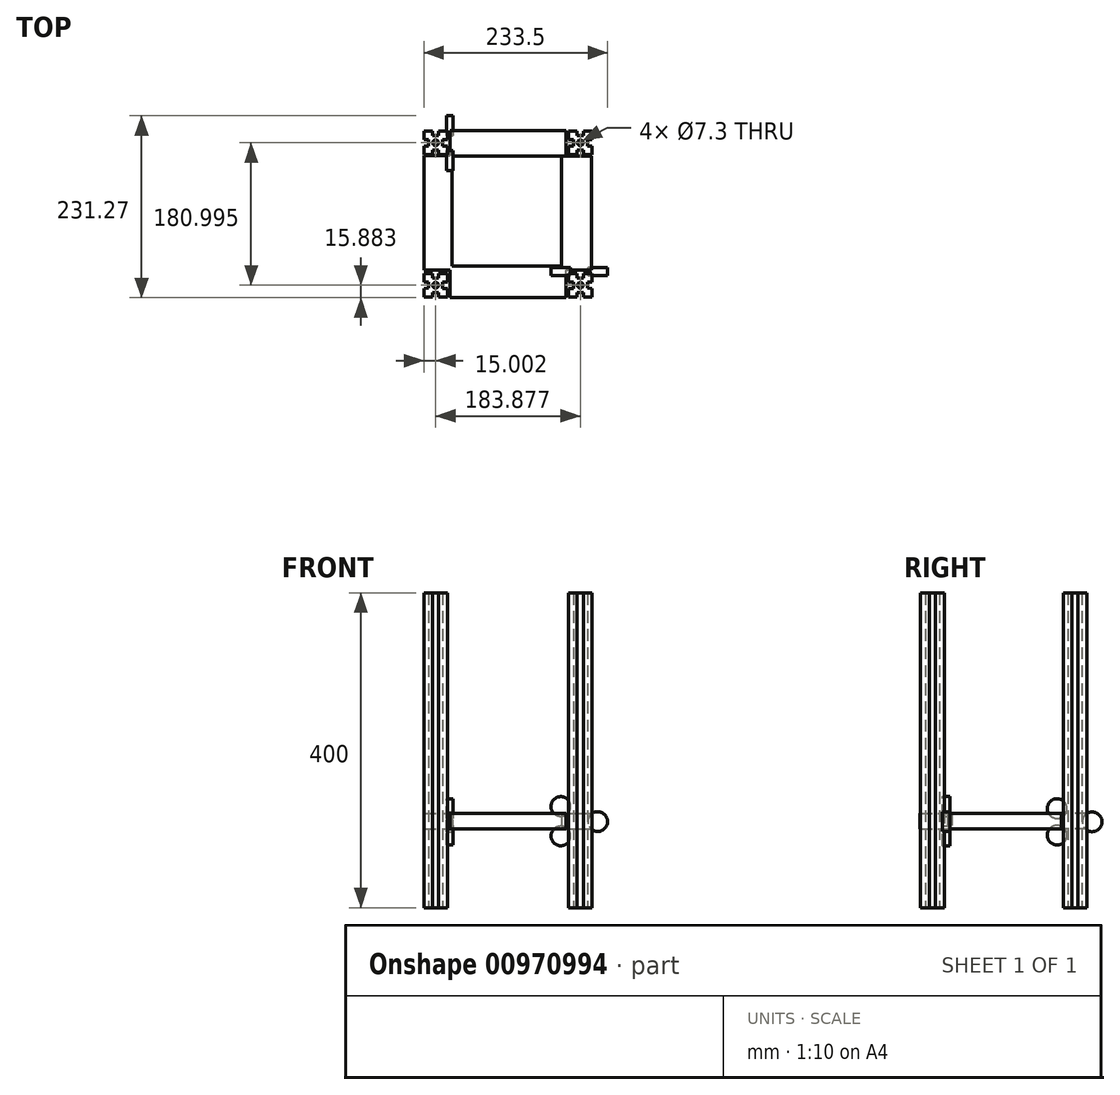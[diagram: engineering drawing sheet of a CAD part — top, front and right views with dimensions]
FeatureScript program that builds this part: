
annotation { "Feature Type Name" : "Feature", "Feature Type Description" : "" }
export const myFeature = defineFeature(function(context is Context, id is Id, definition is map)
    precondition{}
    {
        {
            var Q0;
            Q0=qCreatedBy(makeId("Top.planeOp"),FACE);
            var sketch = newSketch(context, id + "F0", { "sketchPlane" : qUnion([Q0])});
            skLineSegment(sketch, "E0.bottom", {"start": v(87.94, -105.5) * mm, "end": v(76.94, -105.5) * mm});
            skLineSegment(sketch, "E0.top", {"start": v(106.94, -75.5) * mm, "end": v(95.94, -75.5) * mm});
            skLineSegment(sketch, "E1.bottom", {"start": v(82.94, -81.5) * mm, "end": v(100.94, -81.5) * mm});
            skLineSegment(sketch, "E1.top", {"start": v(82.94, -99.5) * mm, "end": v(100.94, -99.5) * mm});
            skLineSegment(sketch, "E1.left", {"start": v(82.94, -81.5) * mm, "end": v(82.94, -99.5) * mm});
            skLineSegment(sketch, "E1.right", {"start": v(100.94, -81.5) * mm, "end": v(100.94, -99.5) * mm});
            skLineSegment(sketch, "E2", {"start": v(82.94, -81.5) * mm, "end": v(100.94, -99.5) * mm, "construction": true});
            skLineSegment(sketch, "E3", {"start": v(100.94, -81.5) * mm, "end": v(82.94, -99.5) * mm, "construction": true});
            skCircle(sketch, "E4", {"center": v(91.94, -90.5) * mm, "radius": 3.65 * mm});
            skLineSegment(sketch, "E5", {"start": v(95.94, -75.5) * mm, "end": v(106.94, -75.5) * mm});
            skPoint(sketch, "E6.start.orphan", {"position": v(91.94, -75.5) * mm});
            skLineSegment(sketch, "E7", {"start": v(76.94, -75.5) * mm, "end": v(87.94, -75.5) * mm});
            skPoint(sketch, "E8.start.orphan", {"position": v(87.94, -105.5) * mm});
            skLineSegment(sketch, "E9", {"start": v(106.94, -105.5) * mm, "end": v(95.94, -105.5) * mm});
            skLineSegment(sketch, "E10", {"start": v(106.94, -75.5) * mm, "end": v(106.94, -86.5) * mm});
            skLineSegment(sketch, "E11", {"start": v(106.94, -105.5) * mm, "end": v(106.94, -94.5) * mm});
            skLineSegment(sketch, "E12", {"start": v(76.94, -75.5) * mm, "end": v(76.94, -86.5) * mm});
            skLineSegment(sketch, "E13", {"start": v(76.94, -94.5) * mm, "end": v(76.94, -105.5) * mm});
            skLineSegment(sketch, "E14", {"start": v(95.94, -75.5) * mm, "end": v(95.94, -81.5) * mm});
            skLineSegment(sketch, "E15", {"start": v(95.94, -81.5) * mm, "end": v(87.94, -81.5) * mm});
            skLineSegment(sketch, "E16", {"start": v(87.94, -81.5) * mm, "end": v(87.94, -75.5) * mm});
            skLineSegment(sketch, "E17", {"start": v(76.94, -86.5) * mm, "end": v(82.94, -86.5) * mm});
            skLineSegment(sketch, "E18", {"start": v(82.94, -86.5) * mm, "end": v(82.94, -94.5) * mm});
            skLineSegment(sketch, "E19", {"start": v(82.94, -94.5) * mm, "end": v(76.94, -94.5) * mm});
            skLineSegment(sketch, "E20", {"start": v(87.94, -99.5) * mm, "end": v(87.94, -105.5) * mm});
            skLineSegment(sketch, "E21", {"start": v(95.94, -105.5) * mm, "end": v(95.94, -99.5) * mm});
            skLineSegment(sketch, "E22", {"start": v(106.94, -94.5) * mm, "end": v(100.94, -94.36) * mm});
            skLineSegment(sketch, "E23", {"start": v(100.94, -94.36) * mm, "end": v(100.94, -86.5) * mm});
            skLineSegment(sketch, "E24", {"start": v(100.94, -86.5) * mm, "end": v(106.94, -86.5) * mm});
            skLineSegment(sketch, "E25.MirrorCS", {"start": v(106.94, 75.5) * mm, "end": v(95.94, 75.5) * mm});
            skLineSegment(sketch, "E26.MirrorCS", {"start": v(100.94, 94.36) * mm, "end": v(100.94, 86.5) * mm});
            skLineSegment(sketch, "E27.MirrorCS", {"start": v(106.94, 105.5) * mm, "end": v(106.94, 94.5) * mm});
            skLineSegment(sketch, "E28.MirrorCS", {"start": v(76.94, 86.5) * mm, "end": v(82.94, 86.5) * mm});
            skLineSegment(sketch, "E29.MirrorCS", {"start": v(76.94, 75.5) * mm, "end": v(87.94, 75.5) * mm});
            skLineSegment(sketch, "E30.MirrorCS", {"start": v(106.94, 105.5) * mm, "end": v(95.94, 105.5) * mm});
            skPoint(sketch, "E31.MirrorP", {"position": v(87.94, 105.5) * mm});
            skLineSegment(sketch, "E32.MirrorCS", {"start": v(95.94, 75.5) * mm, "end": v(106.94, 75.5) * mm});
            skLineSegment(sketch, "E33.MirrorCS", {"start": v(76.94, 75.5) * mm, "end": v(76.94, 86.5) * mm});
            skPoint(sketch, "E34.MirrorP", {"position": v(91.94, 75.5) * mm});
            skLineSegment(sketch, "E35.MirrorCS", {"start": v(82.94, 86.5) * mm, "end": v(82.94, 94.5) * mm});
            skLineSegment(sketch, "E36.MirrorCS", {"start": v(95.94, 105.5) * mm, "end": v(95.94, 99.5) * mm});
            skLineSegment(sketch, "E37.MirrorCS", {"start": v(87.94, 105.5) * mm, "end": v(76.94, 105.5) * mm});
            skLineSegment(sketch, "E38.MirrorCS", {"start": v(106.94, 94.5) * mm, "end": v(100.94, 94.36) * mm});
            skLineSegment(sketch, "E39.MirrorCS", {"start": v(95.94, 75.5) * mm, "end": v(95.94, 81.5) * mm});
            skLineSegment(sketch, "E40.MirrorCS", {"start": v(82.94, 94.5) * mm, "end": v(76.94, 94.5) * mm});
            skLineSegment(sketch, "E41.MirrorCS", {"start": v(82.94, 81.5) * mm, "end": v(100.94, 99.5) * mm, "construction": true});
            skLineSegment(sketch, "E42.MirrorCS", {"start": v(82.94, 99.5) * mm, "end": v(100.94, 99.5) * mm});
            skLineSegment(sketch, "E43.MirrorCS", {"start": v(87.94, 99.5) * mm, "end": v(87.94, 105.5) * mm});
            skLineSegment(sketch, "E44.MirrorCS", {"start": v(76.94, 94.5) * mm, "end": v(76.94, 105.5) * mm});
            skCircle(sketch, "E45.MirrorC", {"center": v(91.94, 90.5) * mm, "radius": 3.65 * mm});
            skLineSegment(sketch, "E46.MirrorCS", {"start": v(95.94, 81.5) * mm, "end": v(87.94, 81.5) * mm});
            skLineSegment(sketch, "E47.MirrorCS", {"start": v(100.94, 81.5) * mm, "end": v(82.94, 99.5) * mm, "construction": true});
            skLineSegment(sketch, "E48.MirrorCS", {"start": v(87.94, 81.5) * mm, "end": v(87.94, 75.5) * mm});
            skLineSegment(sketch, "E49.MirrorCS", {"start": v(100.94, 86.5) * mm, "end": v(106.94, 86.5) * mm});
            skLineSegment(sketch, "E50.MirrorCS", {"start": v(100.94, 81.5) * mm, "end": v(100.94, 99.5) * mm});
            skLineSegment(sketch, "E51.MirrorCS", {"start": v(82.94, 81.5) * mm, "end": v(82.94, 99.5) * mm});
            skLineSegment(sketch, "E52.MirrorCS", {"start": v(82.94, 81.5) * mm, "end": v(100.94, 81.5) * mm});
            skLineSegment(sketch, "E53.MirrorCS", {"start": v(106.94, 75.5) * mm, "end": v(106.94, 86.5) * mm});
            skLineSegment(sketch, "E54.MirrorCS", {"start": v(-100.94, -94.36) * mm, "end": v(-100.94, -86.5) * mm});
            skLineSegment(sketch, "E55.MirrorCS", {"start": v(-106.94, -94.5) * mm, "end": v(-100.94, -94.36) * mm});
            skLineSegment(sketch, "E56.MirrorCS", {"start": v(-100.94, -86.5) * mm, "end": v(-106.94, -86.5) * mm});
            skLineSegment(sketch, "E57.MirrorCS", {"start": v(-100.94, -81.5) * mm, "end": v(-100.94, -99.5) * mm});
            skLineSegment(sketch, "E58.MirrorCS", {"start": v(-82.94, -81.5) * mm, "end": v(-100.94, -81.5) * mm});
            skLineSegment(sketch, "E59.MirrorCS", {"start": v(-106.94, -75.5) * mm, "end": v(-95.94, -75.5) * mm});
            skLineSegment(sketch, "E60.MirrorCS", {"start": v(-76.94, -75.5) * mm, "end": v(-76.94, -86.5) * mm});
            skLineSegment(sketch, "E61.MirrorCS", {"start": v(-106.94, -75.5) * mm, "end": v(-106.94, -86.5) * mm});
            skLineSegment(sketch, "E62.MirrorCS", {"start": v(-95.94, -75.5) * mm, "end": v(-95.94, -81.5) * mm});
            skLineSegment(sketch, "E63.MirrorCS", {"start": v(-95.94, -75.5) * mm, "end": v(-106.94, -75.5) * mm});
            skLineSegment(sketch, "E64.MirrorCS", {"start": v(-82.94, 81.5) * mm, "end": v(-100.94, 81.5) * mm});
            skLineSegment(sketch, "E65.MirrorCS", {"start": v(-76.94, -86.5) * mm, "end": v(-82.94, -86.5) * mm});
            skLineSegment(sketch, "E66.MirrorCS", {"start": v(-76.94, -75.5) * mm, "end": v(-87.94, -75.5) * mm});
            skLineSegment(sketch, "E67.MirrorCS", {"start": v(-87.94, -81.5) * mm, "end": v(-87.94, -75.5) * mm});
            skLineSegment(sketch, "E68.MirrorCS", {"start": v(-95.94, -81.5) * mm, "end": v(-87.94, -81.5) * mm});
            skLineSegment(sketch, "E69.MirrorCS", {"start": v(-82.94, -81.5) * mm, "end": v(-82.94, -99.5) * mm});
            skLineSegment(sketch, "E70.MirrorCS", {"start": v(-106.94, 75.5) * mm, "end": v(-95.94, 75.5) * mm});
            skLineSegment(sketch, "E71.MirrorCS", {"start": v(-95.94, 75.5) * mm, "end": v(-95.94, 81.5) * mm});
            skLineSegment(sketch, "E72.MirrorCS", {"start": v(-82.94, -81.5) * mm, "end": v(-100.94, -99.5) * mm, "construction": true});
            skLineSegment(sketch, "E73.MirrorCS", {"start": v(-95.94, 81.5) * mm, "end": v(-87.94, 81.5) * mm});
            skLineSegment(sketch, "E74.MirrorCS", {"start": v(-100.94, 94.36) * mm, "end": v(-100.94, 86.5) * mm});
            skLineSegment(sketch, "E75.MirrorCS", {"start": v(-82.94, 81.5) * mm, "end": v(-82.94, 99.5) * mm});
            skLineSegment(sketch, "E76.MirrorCS", {"start": v(-76.94, -94.5) * mm, "end": v(-76.94, -105.5) * mm});
            skLineSegment(sketch, "E77.MirrorCS", {"start": v(-82.94, -86.5) * mm, "end": v(-82.94, -94.5) * mm});
            skLineSegment(sketch, "E78.MirrorCS", {"start": v(-82.94, 86.5) * mm, "end": v(-82.94, 94.5) * mm});
            skLineSegment(sketch, "E79.MirrorCS", {"start": v(-100.94, 81.5) * mm, "end": v(-82.94, 99.5) * mm, "construction": true});
            skLineSegment(sketch, "E80.MirrorCS", {"start": v(-100.94, 86.5) * mm, "end": v(-106.94, 86.5) * mm});
            skLineSegment(sketch, "E81.MirrorCS", {"start": v(-106.94, 75.5) * mm, "end": v(-106.94, 86.5) * mm});
            skLineSegment(sketch, "E82.MirrorCS", {"start": v(-106.94, -105.5) * mm, "end": v(-106.94, -94.5) * mm});
            skCircle(sketch, "E83.MirrorC", {"center": v(-91.94, -90.5) * mm, "radius": 3.65 * mm});
            skLineSegment(sketch, "E84.MirrorCS", {"start": v(-82.94, -94.5) * mm, "end": v(-76.94, -94.5) * mm});
            skLineSegment(sketch, "E85.MirrorCS", {"start": v(-100.94, -81.5) * mm, "end": v(-82.94, -99.5) * mm, "construction": true});
            skLineSegment(sketch, "E86.MirrorCS", {"start": v(-95.94, 105.5) * mm, "end": v(-95.94, 99.5) * mm});
            skLineSegment(sketch, "E87.MirrorCS", {"start": v(-106.94, -105.5) * mm, "end": v(-95.94, -105.5) * mm});
            skLineSegment(sketch, "E88.MirrorCS", {"start": v(-100.94, 81.5) * mm, "end": v(-100.94, 99.5) * mm});
            skLineSegment(sketch, "E89.MirrorCS", {"start": v(-82.94, -99.5) * mm, "end": v(-100.94, -99.5) * mm});
            skLineSegment(sketch, "E90.MirrorCS", {"start": v(-95.94, -105.5) * mm, "end": v(-95.94, -99.5) * mm});
            skLineSegment(sketch, "E91.MirrorCS", {"start": v(-87.94, 99.5) * mm, "end": v(-87.94, 105.5) * mm});
            skLineSegment(sketch, "E92.MirrorCS", {"start": v(-87.94, -99.5) * mm, "end": v(-87.94, -105.5) * mm});
            skLineSegment(sketch, "E93.MirrorCS", {"start": v(-87.94, -105.5) * mm, "end": v(-76.94, -105.5) * mm});
            skLineSegment(sketch, "E94.MirrorCS", {"start": v(-87.94, 81.5) * mm, "end": v(-87.94, 75.5) * mm});
            skLineSegment(sketch, "E95.MirrorCS", {"start": v(-106.94, 94.5) * mm, "end": v(-100.94, 94.36) * mm});
            skLineSegment(sketch, "E96.MirrorCS", {"start": v(-82.94, 99.5) * mm, "end": v(-100.94, 99.5) * mm});
            skCircle(sketch, "E97.MirrorC", {"center": v(-91.94, 90.5) * mm, "radius": 3.65 * mm});
            skLineSegment(sketch, "E98.MirrorCS", {"start": v(-82.94, 81.5) * mm, "end": v(-100.94, 99.5) * mm, "construction": true});
            skLineSegment(sketch, "E99.MirrorCS", {"start": v(-76.94, 75.5) * mm, "end": v(-76.94, 86.5) * mm});
            skLineSegment(sketch, "E100.MirrorCS", {"start": v(-76.94, 86.5) * mm, "end": v(-82.94, 86.5) * mm});
            skLineSegment(sketch, "E101.MirrorCS", {"start": v(-87.94, 105.5) * mm, "end": v(-76.94, 105.5) * mm});
            skLineSegment(sketch, "E102.MirrorCS", {"start": v(-106.94, 105.5) * mm, "end": v(-95.94, 105.5) * mm});
            skLineSegment(sketch, "E103.MirrorCS", {"start": v(-95.94, 75.5) * mm, "end": v(-106.94, 75.5) * mm});
            skLineSegment(sketch, "E104.MirrorCS", {"start": v(-106.94, 105.5) * mm, "end": v(-106.94, 94.5) * mm});
            skLineSegment(sketch, "E105.MirrorCS", {"start": v(-76.94, 94.5) * mm, "end": v(-76.94, 105.5) * mm});
            skLineSegment(sketch, "E106.MirrorCS", {"start": v(-82.94, 94.5) * mm, "end": v(-76.94, 94.5) * mm});
            skLineSegment(sketch, "E107.MirrorCS", {"start": v(-76.94, 75.5) * mm, "end": v(-87.94, 75.5) * mm});
            skPoint(sketch, "E108.MirrorP", {"position": v(-87.94, -105.5) * mm});
            skPoint(sketch, "E109.MirrorP", {"position": v(-87.94, 105.5) * mm});
            skPoint(sketch, "E110.MirrorP", {"position": v(-91.94, -75.5) * mm});
            skPoint(sketch, "E111.MirrorP", {"position": v(-91.94, 75.5) * mm});
            skSolve(sketch);
        }
        {
            var Q0;
            {var subQ7=sQuery(id+"F0.wireOp",EDGE,"E86.MirrorCS");var subQ9=sQuery(id+"F0.wireOp",EDGE,"E91.MirrorCS");var subQ11=sQuery(id+"F0.wireOp",EDGE,"E74.MirrorCS");var subQ16=sQuery(id+"F0.wireOp",EDGE,"E94.MirrorCS");var subQ50=sQuery(id+"F0.wireOp",EDGE,"E54.MirrorCS");var subQ51=sQuery(id+"F0.wireOp",EDGE,"E55.MirrorCS");var subQ54=sQuery(id+"F0.wireOp",EDGE,"E56.MirrorCS");var subQ73=sQuery(id+"F0.wireOp",EDGE,"E26.MirrorCS");var subQ81=sQuery(id+"F0.wireOp",EDGE,"E28.MirrorCS");Q0=qUnion([makeQuery(id+"F0.imprint","IMPRINT",FACE,{"disambiguationData":[TD([[makeQuery(id+"F0.imprint","IMPRINT",EDGE,{"derivedFrom":sQuery(id+"F0.wireOp",EDGE,"E9")}),-1.0]])]}),makeQuery(id+"F0.imprint","IMPRINT",FACE,{"disambiguationData":[TD([[makeQuery(id+"F0.imprint","IMPRINT",EDGE,{"derivedFrom":sQuery(id+"F0.wireOp",EDGE,"E0.bottom")}),-1.0]])]}),makeQuery(id+"F0.imprint","IMPRINT",FACE,{"disambiguationData":[TD([[makeQuery(id+"F0.imprint","IMPRINT",EDGE,{"derivedFrom":sQuery(id+"F0.wireOp",EDGE,"E4")}),-1.0]])]}),makeQuery(id+"F0.imprint","IMPRINT",FACE,{"disambiguationData":[TD([[makeQuery(id+"F0.imprint","IMPRINT",EDGE,{"derivedFrom":sQuery(id+"F0.wireOp",EDGE,"E0.top")}),1.0]])]}),makeQuery(id+"F0.imprint","IMPRINT",FACE,{"disambiguationData":[TD([[makeQuery(id+"F0.imprint","IMPRINT",EDGE,{"derivedFrom":sQuery(id+"F0.wireOp",EDGE,"E7")}),-1.0]])]}),makeQuery(id+"F0.imprint","IMPRINT",FACE,{"disambiguationData":[TD([[makeQuery(id+"F0.imprint","IMPRINT",EDGE,{"derivedFrom":subQ73}),-1.0]])]}),makeQuery(id+"F0.imprint","IMPRINT",FACE,{"disambiguationData":[TD([[makeQuery(id+"F0.imprint","IMPRINT",EDGE,{"derivedFrom":sQuery(id+"F0.wireOp",EDGE,"E27.MirrorCS")}),-1.0]])]}),makeQuery(id+"F0.imprint","IMPRINT",FACE,{"disambiguationData":[TD([[makeQuery(id+"F0.imprint","IMPRINT",EDGE,{"derivedFrom":subQ81}),-1.0]])]}),makeQuery(id+"F0.imprint","IMPRINT",FACE,{"disambiguationData":[TD([[makeQuery(id+"F0.imprint","IMPRINT",EDGE,{"derivedFrom":sQuery(id+"F0.wireOp",EDGE,"E25.MirrorCS")}),-1.0]])]}),makeQuery(id+"F0.imprint","IMPRINT",FACE,{"disambiguationData":[TD([[makeQuery(id+"F0.imprint","IMPRINT",EDGE,{"derivedFrom":sQuery(id+"F0.wireOp",EDGE,"E37.MirrorCS")}),1.0]])]}),makeQuery(id+"F0.imprint","IMPRINT",FACE,{"disambiguationData":[TD([[makeQuery(id+"F0.imprint","IMPRINT",EDGE,{"derivedFrom":subQ51}),-1.0]])]}),makeQuery(id+"F0.imprint","IMPRINT",FACE,{"disambiguationData":[TD([[makeQuery(id+"F0.imprint","IMPRINT",EDGE,{"derivedFrom":subQ54}),-1.0]])]}),makeQuery(id+"F0.imprint","IMPRINT",FACE,{"disambiguationData":[TD([[makeQuery(id+"F0.imprint","IMPRINT",EDGE,{"derivedFrom":sQuery(id+"F0.wireOp",EDGE,"E60.MirrorCS")}),-1.0]])]}),makeQuery(id+"F0.imprint","IMPRINT",FACE,{"disambiguationData":[TD([[makeQuery(id+"F0.imprint","IMPRINT",EDGE,{"derivedFrom":sQuery(id+"F0.wireOp",EDGE,"E76.MirrorCS")}),-1.0]])]}),makeQuery(id+"F0.imprint","IMPRINT",FACE,{"disambiguationData":[TD([[makeQuery(id+"F0.imprint","IMPRINT",EDGE,{"derivedFrom":subQ50}),-1.0]])]}),makeQuery(id+"F0.imprint","IMPRINT",FACE,{"disambiguationData":[TD([[makeQuery(id+"F0.imprint","IMPRINT",EDGE,{"derivedFrom":subQ7}),-1.0]])]}),makeQuery(id+"F0.imprint","IMPRINT",FACE,{"disambiguationData":[TD([[makeQuery(id+"F0.imprint","IMPRINT",EDGE,{"derivedFrom":sQuery(id+"F0.wireOp",EDGE,"E70.MirrorCS")}),1.0]])]}),makeQuery(id+"F0.imprint","IMPRINT",FACE,{"disambiguationData":[TD([[makeQuery(id+"F0.imprint","IMPRINT",EDGE,{"derivedFrom":subQ16}),1.0]])]}),makeQuery(id+"F0.imprint","IMPRINT",FACE,{"disambiguationData":[TD([[makeQuery(id+"F0.imprint","IMPRINT",EDGE,{"derivedFrom":subQ9}),-1.0]])]}),makeQuery(id+"F0.imprint","IMPRINT",FACE,{"disambiguationData":[TD([[makeQuery(id+"F0.imprint","IMPRINT",EDGE,{"derivedFrom":subQ11}),1.0]])]})]);}
            extrude(context, id + "F1", {"entities" : qUnion([Q0]), "depth" : 400 * mm, "offsetDistance" : 25 * mm});
        }
        {
            var Q0;
            Q0=qCreatedBy(makeId("Top.planeOp"),FACE);
            var sketch = newSketch(context, id + "F2", { "sketchPlane" : qUnion([Q0])});
            skLineSegment(sketch, "E112.bottom", {"start": v(67.97, 73.3) * mm, "end": v(106.14, 73.3) * mm});
            skLineSegment(sketch, "E112.top", {"start": v(67.97, -71.44) * mm, "end": v(106.14, -71.44) * mm});
            skLineSegment(sketch, "E112.left", {"start": v(67.97, 73.3) * mm, "end": v(67.97, -71.44) * mm});
            skLineSegment(sketch, "E112.right", {"start": v(106.14, 73.3) * mm, "end": v(106.14, -71.44) * mm});
            skLineSegment(sketch, "E113.bottom", {"start": v(-106.7, 74.02) * mm, "end": v(-71.22, 74.02) * mm});
            skLineSegment(sketch, "E113.top", {"start": v(-106.7, -71.44) * mm, "end": v(-71.22, -71.44) * mm});
            skLineSegment(sketch, "E113.left", {"start": v(-106.7, 74.02) * mm, "end": v(-106.7, -71.44) * mm});
            skLineSegment(sketch, "E113.right", {"start": v(-71.22, 74.02) * mm, "end": v(-71.22, -71.44) * mm});
            skLineSegment(sketch, "E114.bottom", {"start": v(-73.9, 105.75) * mm, "end": v(73.7, 105.75) * mm});
            skLineSegment(sketch, "E114.top", {"start": v(-73.9, 73.53) * mm, "end": v(73.7, 73.53) * mm});
            skLineSegment(sketch, "E114.left", {"start": v(-73.9, 105.75) * mm, "end": v(-73.9, 73.53) * mm});
            skLineSegment(sketch, "E114.right", {"start": v(73.7, 105.75) * mm, "end": v(73.7, 73.53) * mm});
            skLineSegment(sketch, "E115.bottom", {"start": v(-73.9, -106.38) * mm, "end": v(73.7, -106.38) * mm});
            skLineSegment(sketch, "E115.top", {"start": v(-73.9, -65.84) * mm, "end": v(73.7, -65.84) * mm});
            skLineSegment(sketch, "E115.left", {"start": v(-73.9, -106.38) * mm, "end": v(-73.9, -65.84) * mm});
            skLineSegment(sketch, "E115.right", {"start": v(73.7, -106.38) * mm, "end": v(73.7, -65.84) * mm});
            skSolve(sketch);
        }
        {
            var Q0;
            Q0 = qSketchRegion(id + "F2", true);
            extrude(context, id + "F3", {"entities" : qUnion([Q0]), "depth" : 120 * mm, "offsetDistance" : 25 * mm, "hasSecondDirection" : true, "secondDirectionOppositeDirection" : false, "secondDirectionDepth" : 100 * mm});
        }
        {
            var Q0;
            Q0=qCreatedBy(makeId("Front.planeOp"),FACE);
            var sketch = newSketch(context, id + "F4", { "sketchPlane" : qUnion([Q0])});
            skCircle(sketch, "E116", {"center": v(67.15, 128.76) * mm, "radius": 12.5 * mm});
            skCircle(sketch, "E117", {"center": v(67.15, 91.3) * mm, "radius": 12.5 * mm});
            skCircle(sketch, "E118", {"center": v(114.06, 109.52) * mm, "radius": 12.5 * mm});
            skSolve(sketch);
        }
        {
            var Q0;
            Q0 = qSketchRegion(id + "F4", true);
            extrude(context, id + "F5", {"entities" : qUnion([Q0]), "depth" : 78 * mm, "offsetDistance" : 25 * mm, "hasSecondDirection" : true, "secondDirectionOppositeDirection" : false, "secondDirectionDepth" : 68 * mm});
        }
        {
            var Q0;
            Q0=qCreatedBy(makeId("Right.planeOp"),FACE);
            var sketch = newSketch(context, id + "F6", { "sketchPlane" : qUnion([Q0])});
            skCircle(sketch, "E119", {"center": v(67.85, 126.06) * mm, "radius": 12.5 * mm});
            skCircle(sketch, "E120", {"center": v(67.85, 92.31) * mm, "radius": 12.5 * mm});
            skCircle(sketch, "E121", {"center": v(112.4, 109.18) * mm, "radius": 12.5 * mm});
            skSolve(sketch);
        }
        {
            var Q0;
            Q0 = qSketchRegion(id + "F6", true);
            extrude(context, id + "F7", {"entities" : qUnion([Q0]), "oppositeDirection" : true, "depth" : 78 * mm, "offsetDistance" : 25 * mm, "hasSecondDirection" : true, "secondDirectionOppositeDirection" : true, "secondDirectionDepth" : 70 * mm});
        }
    });
